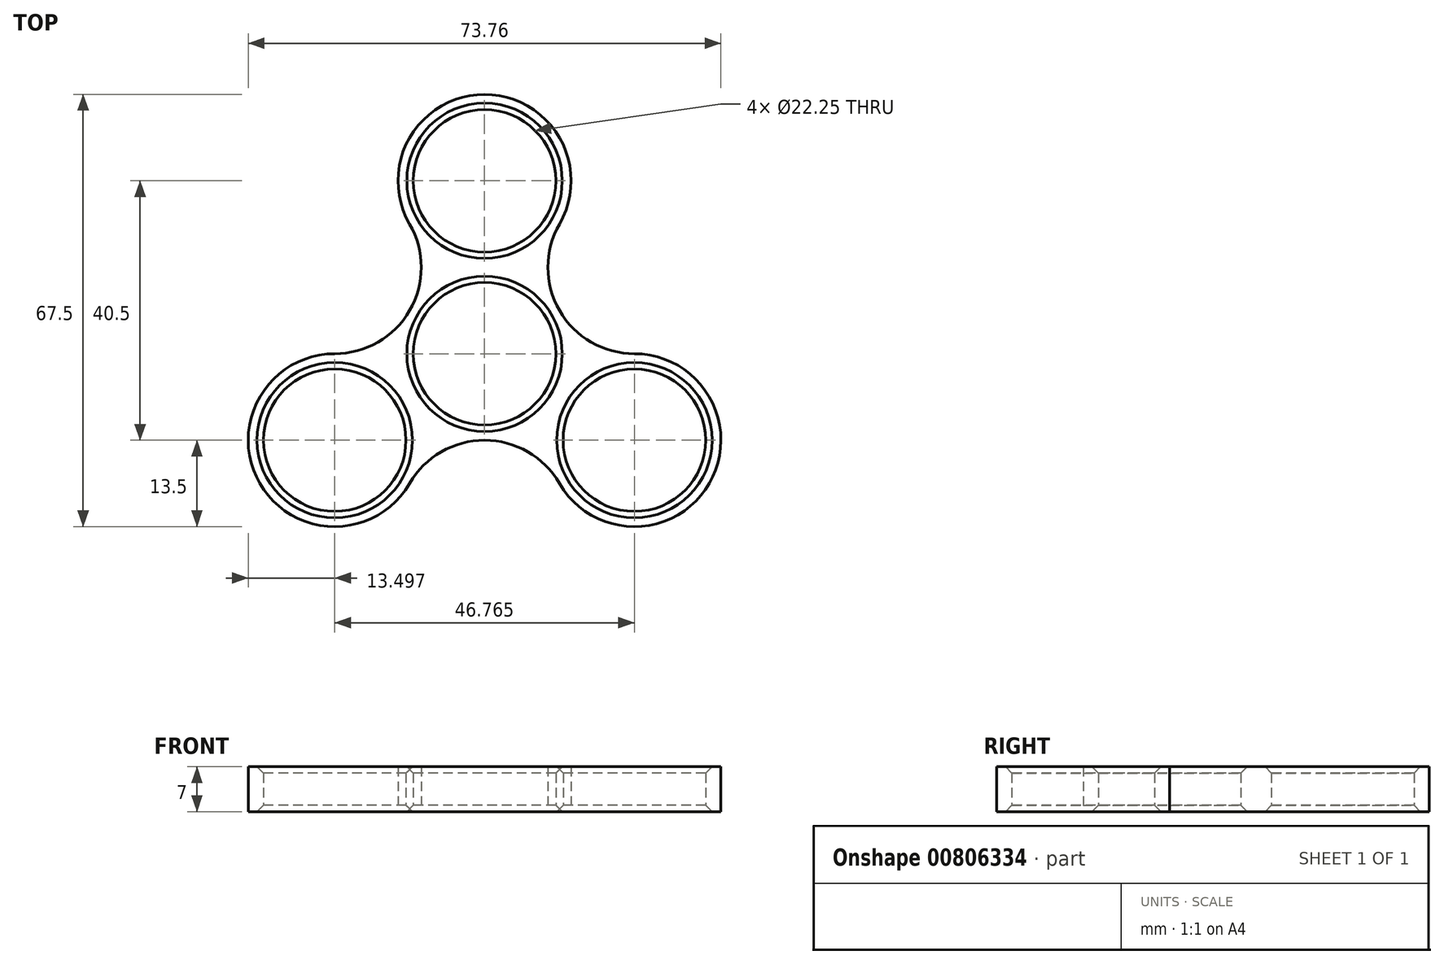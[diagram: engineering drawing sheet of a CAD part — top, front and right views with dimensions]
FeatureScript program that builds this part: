
annotation { "Feature Type Name" : "Feature", "Feature Type Description" : "" }
export const myFeature = defineFeature(function(context is Context, id is Id, definition is map)
    precondition{}
    {
        {
            var Q0;
            Q0=qCreatedBy(makeId("Top.planeOp"),FACE);
            var sketch = newSketch(context, id + "F0", { "sketchPlane" : qUnion([Q0])});
            skCircle(sketch, "E0", {"center": v(0, 0) * mm, "radius": 11.12 * mm});
            skCircle(sketch, "E1", {"center": v(0, 0) * mm, "radius": 13.5 * mm});
            skCircle(sketch, "E2", {"center": v(0, 27) * mm, "radius": 11.12 * mm});
            skCircle(sketch, "E3", {"center": v(0, 27) * mm, "radius": 13.5 * mm});
            skPoint(sketch, "E4.center", {"position": v(0, 0.5) * mm});
            skArc(sketch, "E5.1.1", {"start": v(-23.38, 0) * mm, "mid": v(-11.7, 6.75) * mm, "end": v(-11.7, 20.25) * mm});
            skCircle(sketch, "E5.2.0", {"center": v(-23.38, -13.5) * mm, "radius": 11.12 * mm});
            skCircle(sketch, "E5.2.1", {"center": v(-23.38, -13.5) * mm, "radius": 13.5 * mm});
            skArc(sketch, "E5.3.1", {"start": v(11.7, -20.25) * mm, "mid": v(0, -13.5) * mm, "end": v(-11.7, -20.25) * mm});
            skCircle(sketch, "E5.4.0", {"center": v(23.38, -13.5) * mm, "radius": 11.12 * mm});
            skCircle(sketch, "E5.4.1", {"center": v(23.38, -13.5) * mm, "radius": 13.5 * mm});
            skArc(sketch, "E5.5.1", {"start": v(11.7, 20.25) * mm, "mid": v(11.7, 6.75) * mm, "end": v(23.38, 0) * mm});
            skSolve(sketch);
        }
        {
            var Q0;
            Q0=makeQuery(id+"F0.imprint","IMPRINT",FACE,{"disambiguationData":[TD([[makeQuery(id+"F0.imprint","IMPRINT",EDGE,{"derivedFrom":sQuery(id+"F0.wireOp",EDGE,"E1")}),-1.0]])]});
            var Q1;
            Q1=makeQuery(id+"F0.imprint","IMPRINT",FACE,{"disambiguationData":[TD([[makeQuery(id+"F0.imprint","IMPRINT",EDGE,{"derivedFrom":sQuery(id+"F0.wireOp",EDGE,"c202e4ac-ae93-4b29-baa2-4fd0cf997ff0.1.0")}),-1.0]])]});
            var Q2;
            Q2=makeQuery(id+"F0.imprint","IMPRINT",FACE,{"disambiguationData":[TD([[makeQuery(id+"F0.imprint","IMPRINT",EDGE,{"derivedFrom":sQuery(id+"F0.wireOp",EDGE,"E0")}),-1.0]])]});
            var Q3;
            Q3=makeQuery(id+"F0.imprint","IMPRINT",FACE,{"disambiguationData":[TD([[makeQuery(id+"F0.imprint","IMPRINT",EDGE,{"derivedFrom":sQuery(id+"F0.wireOp",EDGE,"E2")}),-1.0]])]});
            var Q4;
            Q4=makeQuery(id+"F0.imprint","IMPRINT",FACE,{"disambiguationData":[TD([[makeQuery(id+"F0.imprint","IMPRINT",EDGE,{"derivedFrom":sQuery(id+"F0.wireOp",EDGE,"c202e4ac-ae93-4b29-baa2-4fd0cf997ff0.2.0")}),-1.0]])]});
            var Q5;
            Q5=makeQuery(id+"F0.imprint","IMPRINT",FACE,{"disambiguationData":[TD([[makeQuery(id+"F0.imprint","IMPRINT",EDGE,{"derivedFrom":sQuery(id+"F0.wireOp",EDGE,"E5.2.0")}),-1.0]])]});
            var Q6;
            Q6=makeQuery(id+"F0.imprint","IMPRINT",FACE,{"disambiguationData":[TD([[makeQuery(id+"F0.imprint","IMPRINT",EDGE,{"derivedFrom":sQuery(id+"F0.wireOp",EDGE,"E5.4.0")}),-1.0]])]});
            extrude(context, id + "F1", {"entities" : qUnion([Q0, Q1, Q2, Q3, Q4, Q5, Q6]), "endBound" : BoundingType.SYMMETRIC, "depth" : 7 * mm, "offsetDistance" : 25.4 * mm});
        }
        {
            var Q0;
            Q0=makeQuery(id+"F1.opExtrude","CAP_EDGE",EDGE,{"disambiguationData":[OSD([sQuery(id+"F0.wireOp",EDGE,"c202e4ac-ae93-4b29-baa2-4fd0cf997ff0.1.0")])],"isStart":false});
            var Q1;
            Q1=makeQuery(id+"F1.opExtrude","CAP_EDGE",EDGE,{"disambiguationData":[OSD([sQuery(id+"F0.wireOp",EDGE,"E0")])],"isStart":false});
            var Q2;
            Q2=makeQuery(id+"F1.opExtrude","CAP_EDGE",EDGE,{"disambiguationData":[OSD([sQuery(id+"F0.wireOp",EDGE,"c202e4ac-ae93-4b29-baa2-4fd0cf997ff0.2.0")])],"isStart":false});
            var Q3;
            Q3=makeQuery(id+"F1.opExtrude","CAP_EDGE",EDGE,{"disambiguationData":[OSD([sQuery(id+"F0.wireOp",EDGE,"E2")])],"isStart":false});
            var Q4;
            Q4=makeQuery(id+"F1.opExtrude","CAP_EDGE",EDGE,{"disambiguationData":[OSD([sQuery(id+"F0.wireOp",EDGE,"E5.2.0")])],"isStart":false});
            var Q5;
            Q5=makeQuery(id+"F1.opExtrude","CAP_EDGE",EDGE,{"disambiguationData":[OSD([sQuery(id+"F0.wireOp",EDGE,"E5.4.0")])],"isStart":false});
            chamfer(context, id + "F2", {"entities" : qUnion([Q0, Q1, Q2, Q3, Q4, Q5]), "width" : 1 * mm, "tangentPropagation" : true});
        }
        {
            var Q0;
            Q0=makeQuery(id+"F1.opExtrude","CAP_EDGE",EDGE,{"disambiguationData":[OSD([sQuery(id+"F0.wireOp",EDGE,"c202e4ac-ae93-4b29-baa2-4fd0cf997ff0.1.0")])],"isStart":true});
            var Q1;
            Q1=makeQuery(id+"F1.opExtrude","CAP_EDGE",EDGE,{"disambiguationData":[OSD([sQuery(id+"F0.wireOp",EDGE,"E0")])],"isStart":true});
            var Q2;
            Q2=makeQuery(id+"F1.opExtrude","CAP_EDGE",EDGE,{"disambiguationData":[OSD([sQuery(id+"F0.wireOp",EDGE,"c202e4ac-ae93-4b29-baa2-4fd0cf997ff0.2.0")])],"isStart":true});
            var Q3;
            Q3=makeQuery(id+"F1.opExtrude","CAP_EDGE",EDGE,{"disambiguationData":[OSD([sQuery(id+"F0.wireOp",EDGE,"E2")])],"isStart":true});
            var Q4;
            Q4=makeQuery(id+"F1.opExtrude","CAP_EDGE",EDGE,{"disambiguationData":[OSD([sQuery(id+"F0.wireOp",EDGE,"E5.2.0")])],"isStart":true});
            var Q5;
            Q5=makeQuery(id+"F1.opExtrude","CAP_EDGE",EDGE,{"disambiguationData":[OSD([sQuery(id+"F0.wireOp",EDGE,"E5.4.0")])],"isStart":true});
            chamfer(context, id + "F3", {"entities" : qUnion([Q0, Q1, Q2, Q3, Q4, Q5]), "width" : 1 * mm, "tangentPropagation" : true});
        }
    });
